# Revit family: 202_ELO+PTE-1-_
name_source: partatom
category: Air Terminals
units: mm (PartAtom-declared; Revit-internal decimal feet)

## family parameters
Always vertical = Yes
Cut with Voids When Loaded = No
Part Type = Normal
Room Calculation Point = Yes
Round Connector Dimension = Use Diameter
Shared = No
Work Plane-Based = No

## types (8) — shared parameters
CAT0 = Yes
CL_Location_5000 = 5000 mm  [stored 16.4042 ft]
CON1 = No
CON2 = Yes
Description = Extract unit with plenum box, side connection
L_ARR = 400 mm  [stored 1.31234 ft]
Manufacturer = Climecon
QmdConnectorList = 201;D
URL = www.climecon.fi
W1 = 5 mm  [stored 0.0164042 ft]
W_ARR = 400 mm  [stored 1.31234 ft]
XRefLineVPlnId = 7453
YRefLineVPlnId = 7456
magiPartTypeId = 202
magiProductFamilyId = ELO+PTE-1-*
zero-valued in all types: CLBTZ, H_ARR, MC_Default_elevation

## per-type parameters (varying)
| type | BB1 | BB2 | BB3 | BH3 | C | C__ve | D | EF1 | HH1 | HH2 | magiProductId |
| ELO 300x150+PTE 1-200 | 163 mm  [stored 0.534777 ft] | 150 mm  [stored 0.492126 ft] | 200 mm  [stored 0.656168 ft] | 125 mm  [stored 0.410105 ft] | 300 mm  [stored 0.984252 ft] | -300 mm  [stored -0.984252 ft] | 200 mm | 150 mm  [stored 0.492126 ft] | 88 mm  [stored 0.288714 ft] | 75 mm  [stored 0.246063 ft] | ELO+PTE-1-300x150 |
| ELO 800x300+PTE 1-315 | 413 mm  [stored 1.35499 ft] | 400 mm  [stored 1.31234 ft] | 450 mm  [stored 1.47638 ft] | 225 mm  [stored 0.738189 ft] | 500 mm  [stored 1.64042 ft] | -500 mm  [stored -1.64042 ft] | 315 mm | 250 mm  [stored 0.82021 ft] | 163 mm  [stored 0.534777 ft] | 150 mm  [stored 0.492126 ft] | ELO+PTE-1-800x300 |
| ELO 800x200+PTE 1-315 | 413 mm  [stored 1.35499 ft] | 400 mm  [stored 1.31234 ft] | 450 mm  [stored 1.47638 ft] | 178 mm | 420 mm  [stored 1.37795 ft] | -420 mm  [stored -1.37795 ft] | 315 mm | 210 mm  [stored 0.688976 ft] | 113 mm  [stored 0.370735 ft] | 100 mm  [stored 0.328084 ft] | ELO+PTE-1-800x200 |
| ELO 800x150+PTE 1-315 | 413 mm  [stored 1.35499 ft] | 400 mm  [stored 1.31234 ft] | 450 mm  [stored 1.47638 ft] | 178 mm | 420 mm  [stored 1.37795 ft] | -420 mm  [stored -1.37795 ft] | 315 mm | 210 mm  [stored 0.688976 ft] | 88 mm  [stored 0.288714 ft] | 75 mm  [stored 0.246063 ft] | ELO+PTE-1-800x150 |
| ELO 600x150+PTE 1-315 | 313 mm  [stored 1.0269 ft] | 300 mm  [stored 0.984252 ft] | 350 mm  [stored 1.14829 ft] | 178 mm | 420 mm  [stored 1.37795 ft] | -420 mm  [stored -1.37795 ft] | 315 mm | 210 mm  [stored 0.688976 ft] | 88 mm  [stored 0.288714 ft] | 75 mm  [stored 0.246063 ft] | ELO+PTE-1-600x150 |
| ELO 500x300+PTE 1-315 | 263 mm  [stored 0.862861 ft] | 250 mm  [stored 0.82021 ft] | 300 mm  [stored 0.984252 ft] | 178 mm | 420 mm  [stored 1.37795 ft] | -420 mm  [stored -1.37795 ft] | 315 mm | 210 mm  [stored 0.688976 ft] | 163 mm  [stored 0.534777 ft] | 150 mm  [stored 0.492126 ft] | ELO+PTE-1-500x300 |
| ELO 500x200+PTE 1-315 | 263 mm  [stored 0.862861 ft] | 250 mm  [stored 0.82021 ft] | 300 mm  [stored 0.984252 ft] | 178 mm | 420 mm  [stored 1.37795 ft] | -420 mm  [stored -1.37795 ft] | 315 mm | 210 mm  [stored 0.688976 ft] | 113 mm  [stored 0.370735 ft] | 100 mm  [stored 0.328084 ft] | ELO+PTE-1-500x200 |
| ELO 500x150+PTE 1-250 | 263 mm  [stored 0.862861 ft] | 250 mm  [stored 0.82021 ft] | 300 mm  [stored 0.984252 ft] | 145 mm  [stored 0.475722 ft] | 350 mm  [stored 1.14829 ft] | -350 mm  [stored -1.14829 ft] | 250 mm | 175 mm  [stored 0.574147 ft] | 88 mm  [stored 0.288714 ft] | 75 mm  [stored 0.246063 ft] | ELO+PTE-1-500x150 |

note: column(s) folded — value = type name in every type: magiProductCode

note: [stored X ft] marks values corroborated as IEEE doubles in the binary element streams (Revit-internal decimal feet)

## geometry (parser evidence)
native form markers: Sweep x2
no freeform markers — native parametric forms only
